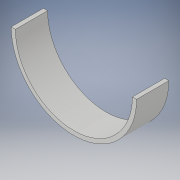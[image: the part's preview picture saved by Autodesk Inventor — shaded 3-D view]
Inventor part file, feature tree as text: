
AUTODESK INVENTOR PART (.ipt)
format: ipt  version: 2017 (Build 210142000, 142)  size: 104,448 bytes
history: native  units: in
note: dims shown in document units (in); Inventor stores cm internally (conversion verified against a paired STEP export)
features: sketch x2, sweep x1
ambient origin geometry x8: Origin, YZ Plane, XZ Plane, XY Plane, X Axis, Y Axis, Z Axis, Center Point
bodies: Solid1 (feature_tree)
feature tree (3):
  sweep  "Sweep1"
  sketch  "Sketch2"  dims[d0=0.5in d1=3.85in]
  sketch  "Sketch3"  dims[d2=0.5in d3=3.85in d6=0.0in d7=0.0in]
